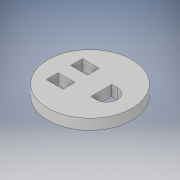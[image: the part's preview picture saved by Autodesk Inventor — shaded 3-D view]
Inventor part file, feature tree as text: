
AUTODESK INVENTOR PART (.ipt)
format: ipt  version: 2018 (Build 220112000, 112)  size: 119,808 bytes
history: native  units: in
note: dims shown in document units (in); Inventor stores cm internally (conversion verified against a paired STEP export)
features: extrude x1, sketch x1
ambient origin geometry x8: Origin, YZ Plane, XZ Plane, XY Plane, X Axis, Y Axis, Z Axis, Center Point
bodies: Solid1 (feature_tree)
feature tree (2):
  extrude  "Extrusion1"  Depth=0.28in
  sketch  "Sketch1"  dims[d0=2.0in d1=0.28in d2=0.28in d3=0.4in d4=0.4in d5=0.5in d7=0.13in d8=0.13in d9=0.0in d10=0.4in d11=0.21in d12=0.21in d13=0.15in d14=0.15in d15=0.25in d16=0.0in]
